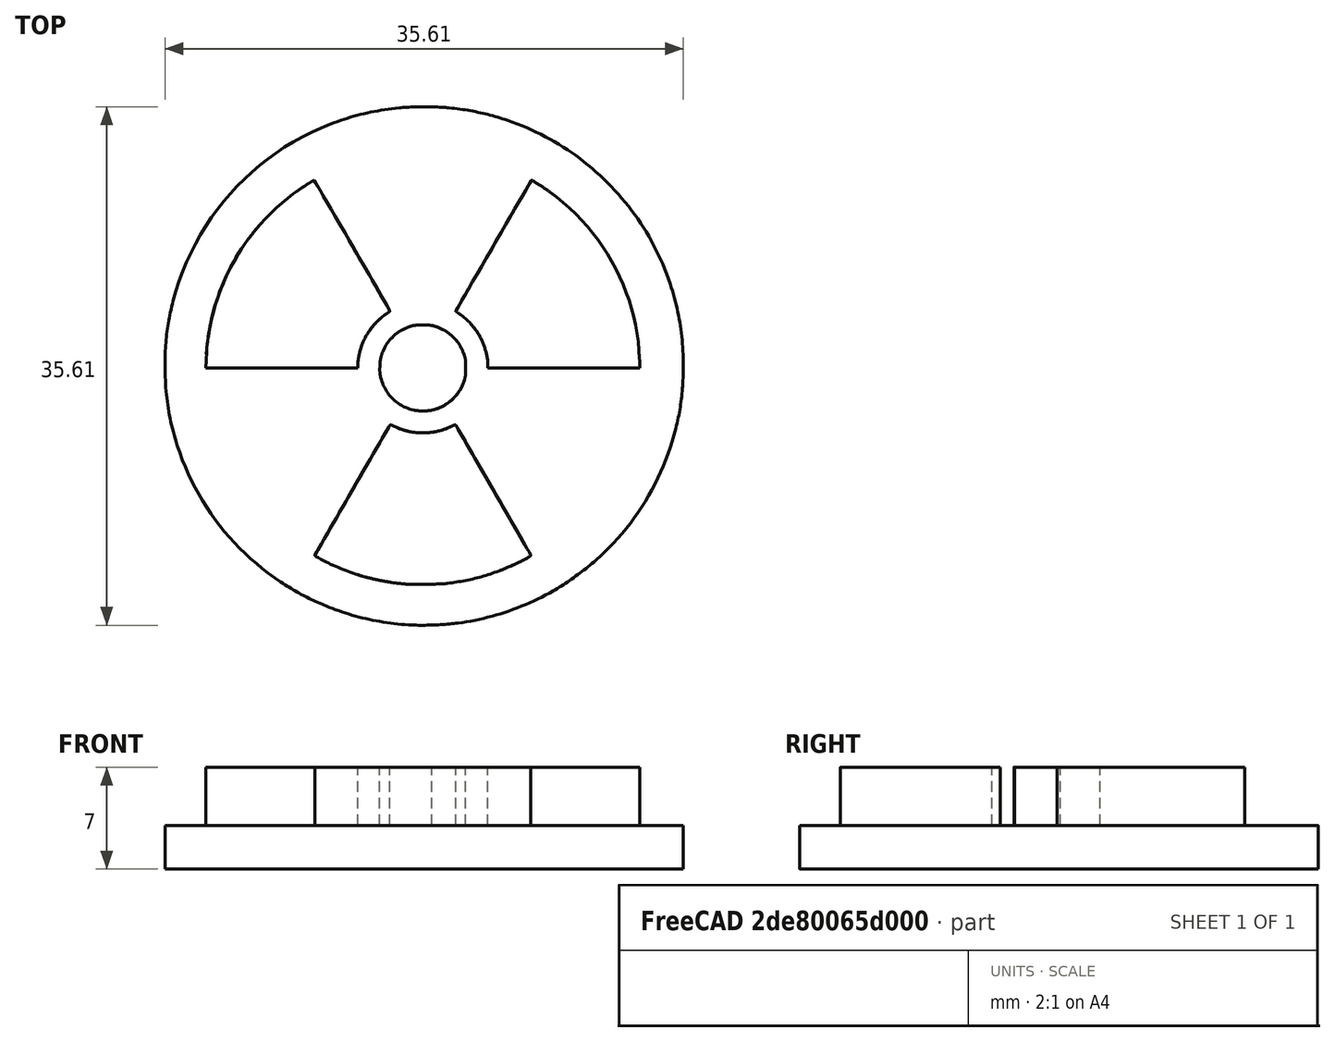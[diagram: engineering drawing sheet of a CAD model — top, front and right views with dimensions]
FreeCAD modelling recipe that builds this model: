
FCSTD DOCUMENT  (FreeCAD 0.19R24291 (Git))
Label: nuclear
License: All rights reserved
LicenseURL: http://en.wikipedia.org/wiki/All_rights_reserved
objects: Part::Feature×5, Part::FeaturePython×4, Part::Extrusion×2, Part::Compound×1, Part::MultiFuse×1
note: 13 computed .brp shape members not serialized (recipe doc carries the construction recipe); baked Part::Feature solids carry a one-line shape summary decoded from their .brp

FEATURE [Part::Feature] path590
  shape: bbox 263.7 x 264.2 x 2e-07 mm, 1 faces, 0 solids (baked)
FEATURE [Part::Feature] path590001
  shape: bbox 110.5 x 81.53 x 2e-07 mm, 1 faces, 0 solids (baked)
FEATURE [Part::Feature] path590002
  shape: bbox 43.83 x 43.89 x 2e-07 mm, 1 faces, 0 solids (baked)
FEATURE [Part::Feature] path590003
  shape: bbox 93.7 x 95.51 x 2e-07 mm, 1 faces, 0 solids (baked)
FEATURE [Part::Feature] path590004
  shape: bbox 93.7 x 95.52 x 2e-07 mm, 1 faces, 0 solids (baked)
FEATURE [Part::Compound] Compound
  Links = -> [path590001,path590002,path590003,path590004]
FEATURE [Part::FeaturePython] Clone  label="path590005"  # Draft clone (typed FeaturePython)
  AttacherType = Attacher::AttachEngine3D
  Fuse = false
  Objects = -> [path590]
  Scale = (0.05,0.05,0.05)
FEATURE [Part::FeaturePython] Clone001  label="Compound001"  # Draft clone (typed FeaturePython)
  AttacherType = Attacher::AttachEngine3D
  Fuse = false
  Objects = -> [Compound]
  Scale = (0.05,0.05,0.05)
FEATURE [Part::FeaturePython] Clone002  label="path590006"  # Draft clone (typed FeaturePython)
  AttacherType = Attacher::AttachEngine3D
  Fuse = false
  Objects = -> [Clone]
  Placement = pos=(-0.16571,-0.354121,0) rot=(0,0,1;0rad)
  Scale = (2.7,2.7,2.7)
FEATURE [Part::FeaturePython] Clone003  label="Compound002"  # Draft clone (typed FeaturePython)
  AttacherType = Attacher::AttachEngine3D
  Fuse = false
  Objects = -> [Clone001]
  Placement = pos=(-0.252587,-0.484832,0) rot=(0,0,1;0rad)
  Scale = (2.7,2.7,2.7)
FEATURE [Part::Extrusion] Extrude
  Base = -> Clone002
  Dir = (0,0,3)
  DirMode = 0
  FaceMakerClass = Part::FaceMakerBullseye
  LengthFwd = 0
  LengthRev = 0
  Solid = true
  Symmetric = false
FEATURE [Part::Extrusion] Extrude001
  Base = -> Clone003
  Dir = (0,0,7)
  DirMode = 0
  FaceMakerClass = Part::FaceMakerBullseye
  LengthFwd = 0
  LengthRev = 0
  Solid = true
  Symmetric = false
FEATURE [Part::MultiFuse] Fusion
  Shapes = -> [Extrude,Extrude001]
